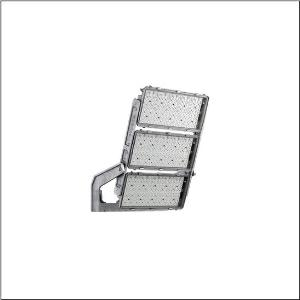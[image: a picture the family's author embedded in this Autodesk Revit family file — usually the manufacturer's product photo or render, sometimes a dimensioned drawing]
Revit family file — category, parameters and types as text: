
# Revit family: floodlight_fl_11_maxi_pro_remote___pl64_5xa779524e01ba_e2b2
name_source: partatom
category: Lighting Fixtures
units: mm (PartAtom-declared; Revit-internal decimal feet)

## family parameters
Cut with Voids When Loaded = No
Host = Face
Light Source = No
Part Type = Normal
Room Calculation Point = No
Round Connector Dimension = Use Diameter
Shared = No

## types (1)
- --- (1 x LED, 107650 lm, 1020.5 W, 5700K)
    Apparent Load = 1020 VA
    CIE Flux Codes = 28 80 98 100 100
    Color Rendering = 90
    Color Temperature = 5700K
    Default Elevation = 1800 mm
    Description = Floodlight FL 11  maxi  pro Remote floodlight; light control with lens of PMMA; cover panel of toughened safety glass, transparent; light distribution: PL64, asymmetric direct distribution, LEDcolour temperature: 5700K, rated luminous flux: 107.650lm, colour rendering: CRI > 90, light colour: 957; luminous efficacy: 106lm/W; brightness control: DMX+RDM; with terminal, 8-pole, max. 2.5mm², mains connection: 220..240V/380..400V AC, 50/60Hz, surge voltage resistance: line to ground: 10kV, ECG replaceable separately, LED unit replaceable without ESD environment, dustproof LED module, dimming range 10..100%; 1021W floodlight with 3x LED unit of diecast aluminium, coated grey; length: 713mm / width: 651mm / height: 338mm; mounting bracket, of diecast aluminium, uncoated, natural, equipment: Longlife, protection rating (complete): IP66; insulation class (complete): insulation class I (protective earthing); certification: CE, ENEC, VDE; ball protection: ball impact resistance with accessories, impact resistance: IK07; only for outdoor installations, rated ambient temperature 10°C, permissible operating ambient temperature: -40..+40°C, permissible storage temperature: -40..+85°C; packaging unit: 1 piece

Light Distribution: PL64
    Height = 320 mm
    Lamp = 1 x LED
    Lamp Light Flux = 107650 lm
    Lamp Power = 1020.5 W
    Lamp count = 1
    Length = 1002 mm
    Luminous efficacy = 105 lm/W
    Manufacturer = Siteco
    ModVariant = No
    Model = 5XA779524E01BA
    Mounting Place = Ceiling
    Mounting Type = Surface mounted
    Number of Poles = 1
    OnlyDefault = Yes
    Power Factor = 1
    Product Name = Floodlight FL 11 maxi pro Remote | PL64
    Product group = floodlight | ceiling mounted
    ProductGroupID = 302
    Protection Class = Protection class I
    Protection Degree = IP 66
    RLX_Detail_Level = 1
    RLX_Emergency_Light_Flux = 0 lm
    RLX_Emergency_Type = 0
    RLX_Emergency_Type_DB = No
    RlxData = <blob elided: 52477 chars, md5=bab5273d>
    Socket = socket
    Standby Power = 0 W
    System Light Flux = 107650 lm
    System Power = 1020 W
    Type Comments = factory setting: luminous flux: 100 % | dim-lin: 255 | 710 mA
    Type Image = l_1006784.jpg
    URL = http://relux.com
    VarID = @adj_066119
    Voltage = 0 V
    Weight = 0.00 kg
    Width = 655 mm

## geometry (parser evidence)
native form markers: Blend x4, Sweep x14
no freeform markers — native parametric forms only
